# Revit family: Haworth_ComposeConnections_TopFeed
name_source: partatom
category: Furniture Systems
revit_build: Autodesk Revit 2018 (Build: 20170223_1515(x64)
units: mm (PartAtom-declared; Revit-internal decimal feet)

## family parameters
Always vertical = Yes
Cut with Voids When Loaded = No
OmniClass Number = 23.40.70.14.64.21
OmniClass Title = Systems Furniture
Part Type = Normal
Room Calculation Point = No
Round Connector Dimension = Use Diameter
Shared = No
Work Plane-Based = No

## types (4) — shared parameters
Assembly Code = E2020500
Description = Haworth - Compose Connections - TopFeed - End of Run Mount
Manufacturer = Haworth
Model = VZET
Revision Number = 3
Size = Verify Final Dim. w/ Haworth
Sustainability Info = http://media.haworth.com
Trim Finish = Haworth _ Paint _ Gray Tone
URL = www.haworth.com
URL - Product = http://www.haworth.com
Warranty = http://www.haworth.com

## per-type parameters (varying)
| type | 10' Ceiling Height | 12' Ceiling Height | Actual Width | Bottom Height | Ceiling Height | End of Run Mount | Pole Length | Post Depth | Top Mount | Top Trim Offset |
| Top Mount - 10' Ceiling Height | Yes | No | 8" | 25 1/2" | 120" | No | 119" | 3 1/4" | Yes | 1" |
| End of Run Mount - 10' Ceiling Height | Yes | No | 3" | 1/2" | 120" | Yes | 119" | 3" | No | 1 3/4" |
| End of Run Mount - 12' Ceiling Height | No | Yes | 3" | 1/2" | 144" | Yes | 138" | 3" | No | 1 3/4" |
| Top Mount - 12' Ceiling Height | No | Yes | 8" | 25 1/2" | 144" | No | 138" | 3 1/4" | Yes | 1" |

## geometry (parser evidence)
native form markers: Sweep x3
no freeform markers — native parametric forms only
